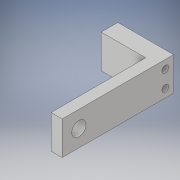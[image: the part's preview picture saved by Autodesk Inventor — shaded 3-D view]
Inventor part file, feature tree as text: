
AUTODESK INVENTOR PART (.ipt)
format: ipt  version: 2019 (Build 230136000, 136)  size: 122,368 bytes
history: native  units: in
note: dims shown in document units (in); Inventor stores cm internally (conversion verified against a paired STEP export)
features: sketch x3, hole x2, projected_geometry x2, extrude x1
ambient origin geometry x8: Origin, YZ Plane, XZ Plane, XY Plane, X Axis, Y Axis, Z Axis, Center Point
bodies: Solid1 (feature_tree)
feature tree (8):
  extrude  "Extrusion1"  Depth=1.25in
  hole  "Hole1"  [1 undecoded]
  hole  "Hole2"  [1 undecoded]
  sketch  "Sketch1"  dims[d0=2.5in d1=1.25in]
  sketch  "Sketch2"  dims[d2=0.375in d3=0.25in]
  projected_geometry  "Projected Loop1"
  sketch  "Sketch3"  dims[d4=0.75in d5=0.0in d6=0.75in d7=0.375in d8=0.375in d9=0.32in d10=0.75in d11=0.375in d12=0.25in d13=0.5635in d14=0.432in d15=0.8108in d16=0.375in d17=0.375in d18=0.1875in d19=0.75in d20=0.1875in d21=0.1875in d22=0.15in d23=0.75in d24=0.375in d25=0.25in d26=0.5635in d27=0.432in d28=0.8108in]
  projected_geometry  "Projected Loop2"
note: 2 required parameter values undecoded (feature->parameter linkage not recoverable at this tier; creation-order binding heuristic only, values carry confidence <= 0.55)
